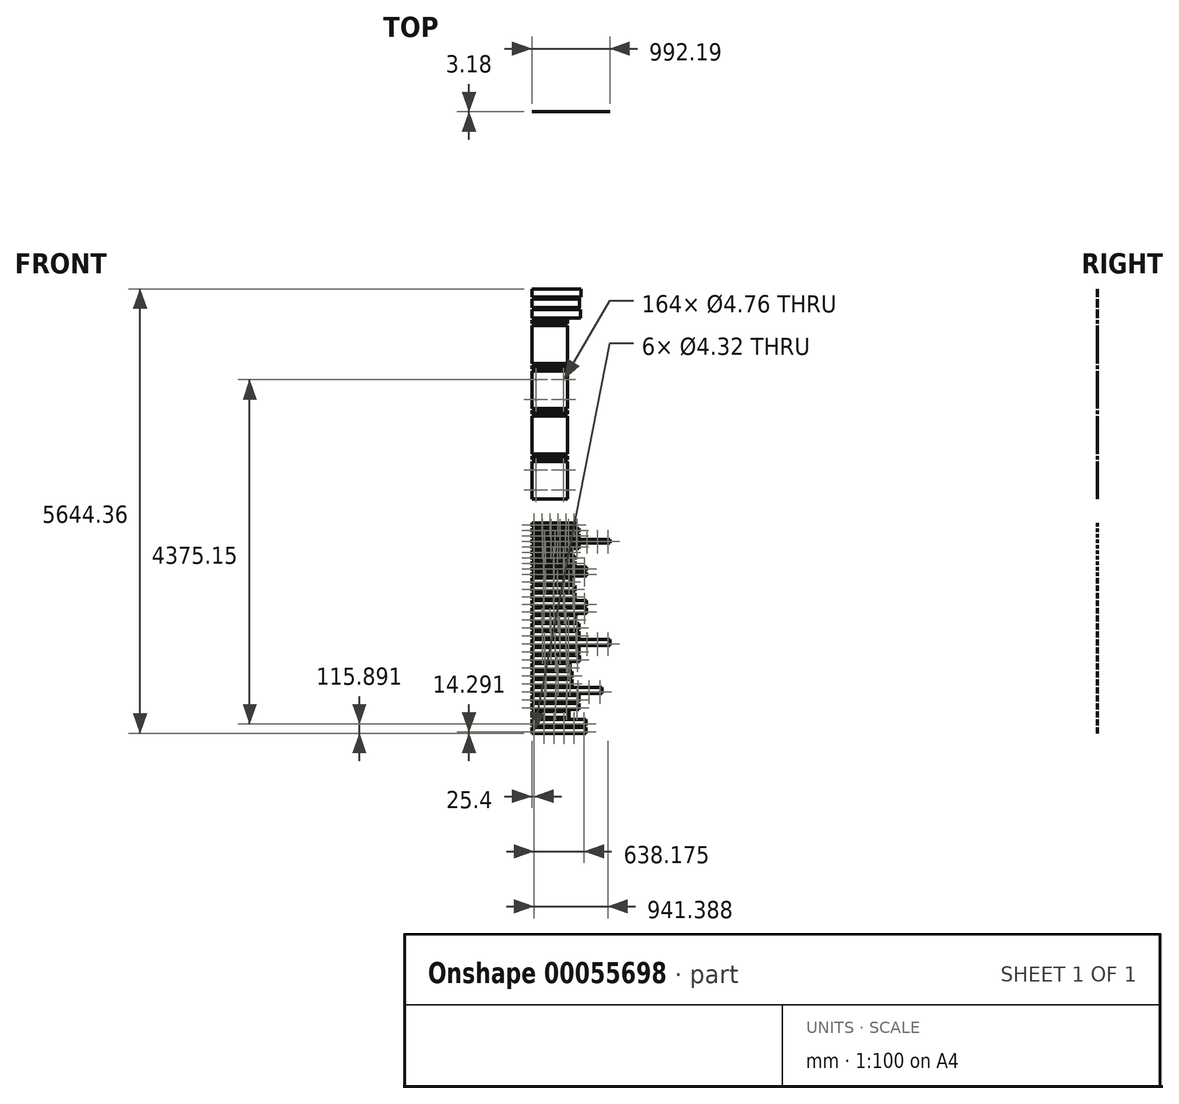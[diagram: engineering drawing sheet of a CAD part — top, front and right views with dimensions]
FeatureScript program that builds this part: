
annotation { "Feature Type Name" : "Feature", "Feature Type Description" : "" }
export const myFeature = defineFeature(function(context is Context, id is Id, definition is map)
    precondition{}
    {
        {
            var Q0;
            Q0=qCreatedBy(makeId("Front.planeOp"),FACE);
            var sketch = newSketch(context, id + "F0", { "sketchPlane" : qUnion([Q0])});
            skLineSegment(sketch, "E0", {"start": v(0, 0) * mm, "end": v(0, -6350) * mm, "construction": true});
            skLineSegment(sketch, "E1.bottom", {"start": v(0, -25.4) * mm, "end": v(621.5, -25.4) * mm});
            skLineSegment(sketch, "E1.top", {"start": v(0, -130.97) * mm, "end": v(621.5, -130.97) * mm});
            skLineSegment(sketch, "E1.left", {"start": v(0, -25.4) * mm, "end": v(0, -130.97) * mm});
            skLineSegment(sketch, "E1.right", {"start": v(621.5, -25.4) * mm, "end": v(621.5, -130.97) * mm});
            skLineSegment(sketch, "E2.bottom", {"start": v(0, -156.37) * mm, "end": v(604.84, -156.37) * mm});
            skLineSegment(sketch, "E2.top", {"start": v(0, -261.94) * mm, "end": v(604.84, -261.94) * mm});
            skLineSegment(sketch, "E2.left", {"start": v(0, -156.37) * mm, "end": v(0, -261.94) * mm});
            skLineSegment(sketch, "E2.right", {"start": v(604.84, -156.37) * mm, "end": v(604.84, -261.94) * mm});
            skLineSegment(sketch, "E3.bottom", {"start": v(0, -287.34) * mm, "end": v(618.33, -287.34) * mm});
            skLineSegment(sketch, "E3.top", {"start": v(0, -392.9) * mm, "end": v(618.33, -392.9) * mm});
            skLineSegment(sketch, "E3.left", {"start": v(0, -287.34) * mm, "end": v(0, -392.9) * mm});
            skLineSegment(sketch, "E3.right", {"start": v(618.33, -287.34) * mm, "end": v(618.33, -392.9) * mm});
            skLineSegment(sketch, "E4.bottom", {"start": v(0, -418.3) * mm, "end": v(454.03, -418.3) * mm});
            skLineSegment(sketch, "E4.top", {"start": v(0, -465.93) * mm, "end": v(454.03, -465.93) * mm});
            skLineSegment(sketch, "E4.left", {"start": v(0, -418.3) * mm, "end": v(0, -465.93) * mm});
            skLineSegment(sketch, "E4.right", {"start": v(454.03, -418.3) * mm, "end": v(454.03, -465.93) * mm});
            skLineSegment(sketch, "E5.bottom", {"start": v(0, -491.33) * mm, "end": v(454.03, -491.33) * mm});
            skLineSegment(sketch, "E5.top", {"start": v(0, -970.76) * mm, "end": v(454.03, -970.76) * mm});
            skLineSegment(sketch, "E5.left", {"start": v(0, -491.33) * mm, "end": v(0, -970.76) * mm});
            skLineSegment(sketch, "E5.right", {"start": v(454.03, -491.33) * mm, "end": v(454.03, -970.76) * mm});
            skLineSegment(sketch, "E6.bottom", {"start": v(0, -996.16) * mm, "end": v(454.03, -996.16) * mm});
            skLineSegment(sketch, "E6.top", {"start": v(0, -1043.78) * mm, "end": v(454.03, -1043.78) * mm});
            skLineSegment(sketch, "E6.left", {"start": v(0, -996.16) * mm, "end": v(0, -1043.78) * mm});
            skLineSegment(sketch, "E6.right", {"start": v(454.03, -996.16) * mm, "end": v(454.03, -1043.78) * mm});
            skLineSegment(sketch, "E7.bottom", {"start": v(0, -1069.18) * mm, "end": v(454.03, -1069.18) * mm});
            skLineSegment(sketch, "E7.top", {"start": v(0, -1542.26) * mm, "end": v(454.03, -1542.26) * mm});
            skLineSegment(sketch, "E7.left", {"start": v(0, -1069.18) * mm, "end": v(0, -1542.26) * mm});
            skLineSegment(sketch, "E7.right", {"start": v(454.03, -1069.18) * mm, "end": v(454.03, -1542.26) * mm});
            skLineSegment(sketch, "E8.bottom", {"start": v(0, -1567.66) * mm, "end": v(454.03, -1567.66) * mm});
            skLineSegment(sketch, "E8.top", {"start": v(0, -1615.28) * mm, "end": v(454.03, -1615.28) * mm});
            skLineSegment(sketch, "E8.left", {"start": v(0, -1567.66) * mm, "end": v(0, -1615.28) * mm});
            skLineSegment(sketch, "E8.right", {"start": v(454.03, -1567.66) * mm, "end": v(454.03, -1615.28) * mm});
            skLineSegment(sketch, "E9.bottom", {"start": v(0, -1640.68) * mm, "end": v(454.03, -1640.68) * mm});
            skLineSegment(sketch, "E9.top", {"start": v(0, -2120.1) * mm, "end": v(454.03, -2120.1) * mm});
            skLineSegment(sketch, "E9.left", {"start": v(0, -1640.68) * mm, "end": v(0, -2120.1) * mm});
            skLineSegment(sketch, "E9.right", {"start": v(454.03, -1640.68) * mm, "end": v(454.03, -2120.1) * mm});
            skLineSegment(sketch, "E10.bottom", {"start": v(0, -2145.5) * mm, "end": v(454.03, -2145.5) * mm});
            skLineSegment(sketch, "E10.top", {"start": v(0, -2193.13) * mm, "end": v(454.03, -2193.13) * mm});
            skLineSegment(sketch, "E10.left", {"start": v(0, -2145.5) * mm, "end": v(0, -2193.13) * mm});
            skLineSegment(sketch, "E10.right", {"start": v(454.03, -2145.5) * mm, "end": v(454.03, -2193.13) * mm});
            skLineSegment(sketch, "E11.bottom", {"start": v(0, -2218.53) * mm, "end": v(454.03, -2218.53) * mm});
            skLineSegment(sketch, "E11.top", {"start": v(0, -2691.6) * mm, "end": v(454.03, -2691.6) * mm});
            skLineSegment(sketch, "E11.left", {"start": v(0, -2218.53) * mm, "end": v(0, -2691.6) * mm});
            skLineSegment(sketch, "E11.right", {"start": v(454.03, -2218.53) * mm, "end": v(454.03, -2691.6) * mm});
            skLineSegment(sketch, "E12.bottom", {"start": v(403.23, -1178.72) * mm, "end": v(50.8, -1178.72) * mm, "construction": true});
            skLineSegment(sketch, "E12.top", {"start": v(403.23, -1432.72) * mm, "end": v(50.8, -1432.72) * mm, "construction": true});
            skLineSegment(sketch, "E12.left", {"start": v(403.23, -1178.72) * mm, "end": v(403.23, -1432.72) * mm, "construction": true});
            skLineSegment(sketch, "E12.right", {"start": v(50.8, -1178.72) * mm, "end": v(50.8, -1432.72) * mm, "construction": true});
            skLineSegment(sketch, "E13.bottom", {"start": v(403.23, -2328.07) * mm, "end": v(50.8, -2328.07) * mm, "construction": true});
            skLineSegment(sketch, "E13.top", {"start": v(403.23, -2582.07) * mm, "end": v(50.8, -2582.07) * mm, "construction": true});
            skLineSegment(sketch, "E13.left", {"start": v(403.22, -2328.07) * mm, "end": v(403.22, -2582.07) * mm, "construction": true});
            skLineSegment(sketch, "E13.right", {"start": v(50.8, -2328.07) * mm, "end": v(50.8, -2582.07) * mm, "construction": true});
            skLineSegment(sketch, "E14", {"start": v(454.03, -1305.72) * mm, "end": v(0, -1305.72) * mm, "construction": true});
            skPoint(sketch, "E15", {"position": v(403.23, -1305.72) * mm});
            skLineSegment(sketch, "E16", {"start": v(454.03, -2455.07) * mm, "end": v(0, -2455.07) * mm, "construction": true});
            skPoint(sketch, "E17", {"position": v(403.23, -2455.07) * mm});
            skCircle(sketch, "E18", {"center": v(403.23, -1178.72) * mm, "radius": 2.38 * mm});
            skCircle(sketch, "E19", {"center": v(403.23, -1432.72) * mm, "radius": 2.38 * mm});
            skCircle(sketch, "E20", {"center": v(403.23, -2328.07) * mm, "radius": 2.38 * mm});
            skCircle(sketch, "E21", {"center": v(403.23, -2582.07) * mm, "radius": 2.38 * mm});
            skCircle(sketch, "E22", {"center": v(50.8, -1178.72) * mm, "radius": 2.38 * mm});
            skCircle(sketch, "E23", {"center": v(50.8, -1432.72) * mm, "radius": 2.38 * mm});
            skCircle(sketch, "E24", {"center": v(50.8, -2328.07) * mm, "radius": 2.38 * mm});
            skCircle(sketch, "E25", {"center": v(50.8, -2582.07) * mm, "radius": 2.38 * mm});
            skLineSegment(sketch, "E26.bottom", {"start": v(0, -4171.16) * mm, "end": v(561.97, -4171.16) * mm});
            skLineSegment(sketch, "E26.top", {"start": v(0, -4247.36) * mm, "end": v(561.97, -4247.36) * mm});
            skLineSegment(sketch, "E26.left", {"start": v(0, -4171.16) * mm, "end": v(0, -4247.36) * mm});
            skLineSegment(sketch, "E26.right", {"start": v(561.97, -4171.16) * mm, "end": v(561.97, -4247.36) * mm});
            skLineSegment(sketch, "E27", {"start": v(25.4, -4233.07) * mm, "end": v(536.57, -4233.07) * mm, "construction": true});
            skCircle(sketch, "E28", {"center": v(25.4, -4233.07) * mm, "radius": 2.38 * mm});
            skCircle(sketch, "E29", {"center": v(127, -4233.07) * mm, "radius": 2.38 * mm});
            skCircle(sketch, "E30", {"center": v(228.6, -4233.07) * mm, "radius": 2.38 * mm});
            skCircle(sketch, "E31", {"center": v(333.37, -4233.07) * mm, "radius": 2.38 * mm});
            skCircle(sketch, "E32", {"center": v(434.97, -4233.07) * mm, "radius": 2.38 * mm});
            skCircle(sketch, "E33", {"center": v(536.57, -4233.07) * mm, "radius": 2.38 * mm});
            skLineSegment(sketch, "E34.bottom", {"start": v(0, -4272.76) * mm, "end": v(596.9, -4272.76) * mm});
            skLineSegment(sketch, "E34.top", {"start": v(0, -4348.96) * mm, "end": v(596.9, -4348.96) * mm});
            skLineSegment(sketch, "E34.left", {"start": v(0, -4272.76) * mm, "end": v(0, -4348.96) * mm});
            skLineSegment(sketch, "E34.right", {"start": v(596.9, -4272.76) * mm, "end": v(596.9, -4348.96) * mm});
            skLineSegment(sketch, "E35", {"start": v(25.4, -4334.67) * mm, "end": v(571.5, -4334.67) * mm, "construction": true});
            skCircle(sketch, "E36", {"center": v(25.4, -4334.67) * mm, "radius": 2.38 * mm});
            skCircle(sketch, "E37", {"center": v(134.94, -4334.67) * mm, "radius": 2.38 * mm});
            skCircle(sketch, "E38", {"center": v(244.47, -4334.67) * mm, "radius": 2.38 * mm});
            skCircle(sketch, "E39", {"center": v(571.5, -4334.67) * mm, "radius": 2.38 * mm});
            skCircle(sketch, "E40", {"center": v(461.96, -4334.67) * mm, "radius": 2.38 * mm});
            skCircle(sketch, "E41", {"center": v(352.42, -4334.67) * mm, "radius": 2.38 * mm});
            skLineSegment(sketch, "E42.bottom", {"start": v(0, -4374.36) * mm, "end": v(598.49, -4374.36) * mm});
            skLineSegment(sketch, "E42.top", {"start": v(0, -4450.56) * mm, "end": v(598.49, -4450.56) * mm});
            skLineSegment(sketch, "E42.left", {"start": v(0, -4374.36) * mm, "end": v(0, -4450.56) * mm});
            skLineSegment(sketch, "E42.right", {"start": v(598.49, -4374.36) * mm, "end": v(598.49, -4450.56) * mm});
            skLineSegment(sketch, "E43", {"start": v(25.4, -4436.27) * mm, "end": v(573.09, -4436.27) * mm, "construction": true});
            skCircle(sketch, "E44", {"center": v(25.4, -4436.27) * mm, "radius": 2.38 * mm});
            skCircle(sketch, "E45", {"center": v(134.94, -4436.27) * mm, "radius": 2.38 * mm});
            skCircle(sketch, "E46", {"center": v(244.47, -4436.27) * mm, "radius": 2.38 * mm});
            skCircle(sketch, "E47", {"center": v(354.01, -4436.27) * mm, "radius": 2.38 * mm});
            skCircle(sketch, "E48", {"center": v(463.55, -4436.27) * mm, "radius": 2.38 * mm});
            skCircle(sketch, "E49", {"center": v(573.09, -4436.27) * mm, "radius": 2.38 * mm});
            skLineSegment(sketch, "E50.bottom", {"start": v(0, -4475.96) * mm, "end": v(992.19, -4475.96) * mm});
            skLineSegment(sketch, "E50.top", {"start": v(0, -4552.16) * mm, "end": v(992.19, -4552.16) * mm});
            skLineSegment(sketch, "E50.left", {"start": v(0, -4475.96) * mm, "end": v(0, -4552.16) * mm});
            skLineSegment(sketch, "E50.right", {"start": v(992.19, -4475.96) * mm, "end": v(992.19, -4552.16) * mm});
            skLineSegment(sketch, "E51", {"start": v(25.4, -4537.87) * mm, "end": v(966.79, -4537.87) * mm, "construction": true});
            skCircle(sketch, "E52", {"center": v(25.4, -4537.87) * mm, "radius": 2.38 * mm});
            skCircle(sketch, "E53", {"center": v(160.34, -4537.87) * mm, "radius": 2.38 * mm});
            skCircle(sketch, "E54", {"center": v(295.27, -4537.87) * mm, "radius": 2.38 * mm});
            skCircle(sketch, "E55", {"center": v(430.21, -4537.87) * mm, "radius": 2.38 * mm});
            skCircle(sketch, "E56", {"center": v(966.79, -4537.87) * mm, "radius": 2.38 * mm});
            skCircle(sketch, "E57", {"center": v(831.85, -4537.87) * mm, "radius": 2.38 * mm});
            skCircle(sketch, "E58", {"center": v(696.91, -4537.87) * mm, "radius": 2.38 * mm});
            skCircle(sketch, "E59", {"center": v(561.97, -4537.87) * mm, "radius": 2.38 * mm});
            skLineSegment(sketch, "E60.bottom", {"start": v(0, -4577.56) * mm, "end": v(595.31, -4577.56) * mm});
            skLineSegment(sketch, "E60.top", {"start": v(0, -4653.76) * mm, "end": v(595.31, -4653.76) * mm});
            skLineSegment(sketch, "E60.left", {"start": v(0, -4577.56) * mm, "end": v(0, -4653.76) * mm});
            skLineSegment(sketch, "E60.right", {"start": v(595.31, -4577.56) * mm, "end": v(595.31, -4653.76) * mm});
            skLineSegment(sketch, "E61", {"start": v(25.4, -4639.47) * mm, "end": v(569.91, -4639.47) * mm, "construction": true});
            skCircle(sketch, "E62", {"center": v(25.4, -4639.47) * mm, "radius": 2.38 * mm});
            skCircle(sketch, "E63", {"center": v(133.35, -4639.47) * mm, "radius": 2.38 * mm});
            skCircle(sketch, "E64", {"center": v(241.3, -4639.47) * mm, "radius": 2.38 * mm});
            skCircle(sketch, "E65", {"center": v(569.91, -4639.47) * mm, "radius": 2.38 * mm});
            skCircle(sketch, "E66", {"center": v(461.96, -4639.47) * mm, "radius": 2.38 * mm});
            skCircle(sketch, "E67", {"center": v(354.01, -4639.47) * mm, "radius": 2.38 * mm});
            skLineSegment(sketch, "E68.bottom", {"start": v(0, -4679.16) * mm, "end": v(604.84, -4679.16) * mm});
            skLineSegment(sketch, "E68.top", {"start": v(0, -4755.36) * mm, "end": v(604.84, -4755.36) * mm});
            skLineSegment(sketch, "E68.left", {"start": v(0, -4679.16) * mm, "end": v(0, -4755.36) * mm});
            skLineSegment(sketch, "E68.right", {"start": v(604.84, -4679.16) * mm, "end": v(604.84, -4755.36) * mm});
            skLineSegment(sketch, "E69", {"start": v(25.4, -4741.07) * mm, "end": v(579.44, -4741.07) * mm, "construction": true});
            skCircle(sketch, "E70", {"center": v(25.4, -4741.07) * mm, "radius": 2.38 * mm});
            skCircle(sketch, "E71", {"center": v(163.51, -4741.07) * mm, "radius": 2.38 * mm});
            skCircle(sketch, "E72", {"center": v(302.42, -4741.07) * mm, "radius": 2.38 * mm});
            skCircle(sketch, "E73", {"center": v(441.32, -4741.07) * mm, "radius": 2.38 * mm});
            skCircle(sketch, "E74", {"center": v(579.44, -4741.07) * mm, "radius": 2.38 * mm});
            skLineSegment(sketch, "E75", {"start": v(163.51, -4715.67) * mm, "end": v(302.42, -4715.67) * mm, "construction": true});
            skLineSegment(sketch, "E76", {"start": v(302.42, -4715.67) * mm, "end": v(441.32, -4715.67) * mm, "construction": true});
            skLineSegment(sketch, "E77.bottom", {"start": v(0, -4780.76) * mm, "end": v(484.19, -4780.76) * mm});
            skLineSegment(sketch, "E77.top", {"start": v(0, -4856.96) * mm, "end": v(484.19, -4856.96) * mm});
            skLineSegment(sketch, "E77.left", {"start": v(0, -4780.76) * mm, "end": v(0, -4856.96) * mm});
            skLineSegment(sketch, "E77.right", {"start": v(484.19, -4780.76) * mm, "end": v(484.19, -4856.96) * mm});
            skLineSegment(sketch, "E78", {"start": v(25.4, -4842.67) * mm, "end": v(458.79, -4842.67) * mm, "construction": true});
            skCircle(sketch, "E79", {"center": v(25.4, -4842.67) * mm, "radius": 2.38 * mm});
            skCircle(sketch, "E80", {"center": v(168.27, -4842.67) * mm, "radius": 2.38 * mm});
            skCircle(sketch, "E81", {"center": v(315.91, -4842.67) * mm, "radius": 2.38 * mm});
            skCircle(sketch, "E82", {"center": v(458.79, -4842.67) * mm, "radius": 2.38 * mm});
            skLineSegment(sketch, "E83.bottom", {"start": v(0, -4882.36) * mm, "end": v(511.17, -4882.36) * mm});
            skLineSegment(sketch, "E83.top", {"start": v(0, -4958.56) * mm, "end": v(511.17, -4958.56) * mm});
            skLineSegment(sketch, "E83.left", {"start": v(0, -4882.36) * mm, "end": v(0, -4958.56) * mm});
            skLineSegment(sketch, "E83.right", {"start": v(511.17, -4882.36) * mm, "end": v(511.17, -4958.56) * mm});
            skLineSegment(sketch, "E84", {"start": v(25.4, -4944.27) * mm, "end": v(485.77, -4944.27) * mm, "construction": true});
            skCircle(sketch, "E85", {"center": v(25.4, -4944.27) * mm, "radius": 2.38 * mm});
            skCircle(sketch, "E86", {"center": v(177.8, -4944.27) * mm, "radius": 2.38 * mm});
            skCircle(sketch, "E87", {"center": v(333.37, -4944.27) * mm, "radius": 2.38 * mm});
            skCircle(sketch, "E88", {"center": v(485.77, -4944.27) * mm, "radius": 2.38 * mm});
            skLineSegment(sketch, "E89.bottom", {"start": v(0, -4983.96) * mm, "end": v(511.17, -4983.96) * mm});
            skLineSegment(sketch, "E89.top", {"start": v(0, -5060.16) * mm, "end": v(511.17, -5060.16) * mm});
            skLineSegment(sketch, "E89.left", {"start": v(0, -4983.96) * mm, "end": v(0, -5060.16) * mm});
            skLineSegment(sketch, "E89.right", {"start": v(511.17, -4983.96) * mm, "end": v(511.17, -5060.16) * mm});
            skLineSegment(sketch, "E90", {"start": v(25.4, -5045.87) * mm, "end": v(485.77, -5045.87) * mm, "construction": true});
            skCircle(sketch, "E91", {"center": v(25.4, -5045.87) * mm, "radius": 2.38 * mm});
            skCircle(sketch, "E92", {"center": v(485.77, -5045.87) * mm, "radius": 2.38 * mm});
            skCircle(sketch, "E93", {"center": v(333.37, -5045.87) * mm, "radius": 2.38 * mm});
            skCircle(sketch, "E94", {"center": v(177.8, -5045.87) * mm, "radius": 2.38 * mm});
            skLineSegment(sketch, "E95.bottom", {"start": v(0, -5085.56) * mm, "end": v(889, -5085.56) * mm});
            skLineSegment(sketch, "E95.top", {"start": v(0, -5161.76) * mm, "end": v(889, -5161.76) * mm});
            skLineSegment(sketch, "E95.left", {"start": v(0, -5085.56) * mm, "end": v(0, -5161.76) * mm});
            skLineSegment(sketch, "E95.right", {"start": v(889, -5085.56) * mm, "end": v(889, -5161.76) * mm});
            skLineSegment(sketch, "E96", {"start": v(25.4, -5147.47) * mm, "end": v(863.6, -5147.47) * mm, "construction": true});
            skCircle(sketch, "E97", {"center": v(25.4, -5147.47) * mm, "radius": 2.38 * mm});
            skCircle(sketch, "E98", {"center": v(165.1, -5147.47) * mm, "radius": 2.38 * mm});
            skCircle(sketch, "E99", {"center": v(304.8, -5147.47) * mm, "radius": 2.38 * mm});
            skCircle(sketch, "E100", {"center": v(444.5, -5147.47) * mm, "radius": 2.38 * mm});
            skCircle(sketch, "E101", {"center": v(584.2, -5147.47) * mm, "radius": 2.38 * mm});
            skCircle(sketch, "E102", {"center": v(723.9, -5147.47) * mm, "radius": 2.38 * mm});
            skCircle(sketch, "E103", {"center": v(863.6, -5147.47) * mm, "radius": 2.38 * mm});
            skLineSegment(sketch, "E104", {"start": v(304.8, -5122.07) * mm, "end": v(444.5, -5122.07) * mm, "construction": true});
            skLineSegment(sketch, "E105", {"start": v(444.5, -5122.07) * mm, "end": v(584.2, -5122.07) * mm, "construction": true});
            skLineSegment(sketch, "E106.bottom", {"start": v(0, -5187.16) * mm, "end": v(600.07, -5187.16) * mm});
            skLineSegment(sketch, "E106.top", {"start": v(0, -5263.36) * mm, "end": v(600.07, -5263.36) * mm});
            skLineSegment(sketch, "E106.left", {"start": v(0, -5187.16) * mm, "end": v(0, -5263.36) * mm});
            skLineSegment(sketch, "E106.right", {"start": v(600.07, -5187.16) * mm, "end": v(600.07, -5263.36) * mm});
            skLineSegment(sketch, "E107", {"start": v(25.4, -5249.07) * mm, "end": v(574.67, -5249.07) * mm, "construction": true});
            skCircle(sketch, "E108", {"center": v(25.4, -5249.07) * mm, "radius": 2.38 * mm});
            skCircle(sketch, "E109", {"center": v(161.92, -5249.07) * mm, "radius": 2.38 * mm});
            skCircle(sketch, "E110", {"center": v(300.04, -5249.07) * mm, "radius": 2.38 * mm});
            skCircle(sketch, "E111", {"center": v(438.15, -5249.07) * mm, "radius": 2.38 * mm});
            skCircle(sketch, "E112", {"center": v(574.67, -5249.07) * mm, "radius": 2.38 * mm});
            skLineSegment(sketch, "E113", {"start": v(161.92, -5223.67) * mm, "end": v(300.04, -5223.67) * mm, "construction": true});
            skLineSegment(sketch, "E114", {"start": v(300.04, -5223.67) * mm, "end": v(438.15, -5223.67) * mm, "construction": true});
            skLineSegment(sketch, "E115.bottom", {"start": v(0, -5288.76) * mm, "end": v(600.07, -5288.76) * mm});
            skLineSegment(sketch, "E115.top", {"start": v(0, -5364.96) * mm, "end": v(600.07, -5364.96) * mm});
            skLineSegment(sketch, "E115.left", {"start": v(0, -5288.76) * mm, "end": v(0, -5364.96) * mm});
            skLineSegment(sketch, "E115.right", {"start": v(600.07, -5288.76) * mm, "end": v(600.07, -5364.96) * mm});
            skLineSegment(sketch, "E116", {"start": v(25.4, -5350.67) * mm, "end": v(574.67, -5350.67) * mm, "construction": true});
            skCircle(sketch, "E117", {"center": v(25.4, -5350.67) * mm, "radius": 2.38 * mm});
            skCircle(sketch, "E118", {"center": v(161.92, -5350.67) * mm, "radius": 2.38 * mm});
            skCircle(sketch, "E119", {"center": v(300.04, -5350.67) * mm, "radius": 2.38 * mm});
            skCircle(sketch, "E120", {"center": v(438.15, -5350.67) * mm, "radius": 2.38 * mm});
            skCircle(sketch, "E121", {"center": v(574.67, -5350.67) * mm, "radius": 2.38 * mm});
            skLineSegment(sketch, "E122", {"start": v(161.92, -5325.27) * mm, "end": v(300.04, -5325.27) * mm, "construction": true});
            skLineSegment(sketch, "E123", {"start": v(300.04, -5325.27) * mm, "end": v(438.15, -5325.27) * mm, "construction": true});
            skLineSegment(sketch, "E124.bottom", {"start": v(0, -5390.36) * mm, "end": v(473.07, -5390.36) * mm});
            skLineSegment(sketch, "E124.top", {"start": v(0, -5466.56) * mm, "end": v(473.07, -5466.56) * mm});
            skLineSegment(sketch, "E124.left", {"start": v(0, -5390.36) * mm, "end": v(0, -5466.56) * mm});
            skLineSegment(sketch, "E124.right", {"start": v(473.07, -5390.36) * mm, "end": v(473.07, -5466.56) * mm});
            skLineSegment(sketch, "E125.bottom", {"start": v(0, -5491.96) * mm, "end": v(688.97, -5491.96) * mm});
            skLineSegment(sketch, "E125.top", {"start": v(0, -5568.16) * mm, "end": v(688.97, -5568.16) * mm});
            skLineSegment(sketch, "E125.left", {"start": v(0, -5491.96) * mm, "end": v(0, -5568.16) * mm});
            skLineSegment(sketch, "E125.right", {"start": v(688.97, -5491.96) * mm, "end": v(688.97, -5568.16) * mm});
            skLineSegment(sketch, "E126", {"start": v(25.4, -5553.87) * mm, "end": v(663.57, -5553.87) * mm, "construction": true});
            skCircle(sketch, "E127", {"center": v(25.4, -5553.87) * mm, "radius": 2.38 * mm});
            skCircle(sketch, "E128", {"center": v(663.57, -5553.87) * mm, "radius": 2.38 * mm});
            skCircle(sketch, "E129", {"center": v(152.4, -5553.87) * mm, "radius": 2.38 * mm});
            skCircle(sketch, "E130", {"center": v(279.4, -5553.87) * mm, "radius": 2.38 * mm});
            skCircle(sketch, "E131", {"center": v(409.57, -5553.87) * mm, "radius": 2.38 * mm});
            skCircle(sketch, "E132", {"center": v(536.57, -5553.87) * mm, "radius": 2.38 * mm});
            skLineSegment(sketch, "E133.bottom", {"start": v(0, -5593.56) * mm, "end": v(688.97, -5593.56) * mm});
            skLineSegment(sketch, "E133.top", {"start": v(0, -5669.76) * mm, "end": v(688.97, -5669.76) * mm});
            skLineSegment(sketch, "E133.left", {"start": v(0, -5593.56) * mm, "end": v(0, -5669.76) * mm});
            skLineSegment(sketch, "E133.right", {"start": v(688.98, -5593.56) * mm, "end": v(688.98, -5669.76) * mm});
            skLineSegment(sketch, "E134", {"start": v(25.4, -5655.47) * mm, "end": v(663.57, -5655.47) * mm, "construction": true});
            skCircle(sketch, "E135", {"center": v(25.4, -5655.47) * mm, "radius": 2.16 * mm});
            skCircle(sketch, "E136", {"center": v(663.57, -5655.47) * mm, "radius": 2.16 * mm});
            skCircle(sketch, "E137", {"center": v(152.4, -5655.47) * mm, "radius": 2.16 * mm});
            skCircle(sketch, "E138", {"center": v(279.4, -5655.47) * mm, "radius": 2.16 * mm});
            skCircle(sketch, "E139", {"center": v(409.57, -5655.47) * mm, "radius": 2.16 * mm});
            skCircle(sketch, "E140", {"center": v(536.57, -5655.47) * mm, "radius": 2.16 * mm});
            skLineSegment(sketch, "E141.bottom", {"start": v(0, -2996.4) * mm, "end": v(561.97, -2996.4) * mm});
            skLineSegment(sketch, "E141.top", {"start": v(0, -3040.86) * mm, "end": v(561.97, -3040.86) * mm});
            skLineSegment(sketch, "E141.left", {"start": v(0, -2996.4) * mm, "end": v(0, -3040.86) * mm});
            skLineSegment(sketch, "E141.right", {"start": v(561.97, -2996.4) * mm, "end": v(561.97, -3040.86) * mm});
            skLineSegment(sketch, "E142", {"start": v(25.4, -3026.57) * mm, "end": v(536.57, -3026.57) * mm, "construction": true});
            skCircle(sketch, "E143", {"center": v(25.4, -3026.57) * mm, "radius": 2.38 * mm});
            skCircle(sketch, "E144", {"center": v(127, -3026.57) * mm, "radius": 2.38 * mm});
            skCircle(sketch, "E145", {"center": v(228.6, -3026.57) * mm, "radius": 2.38 * mm});
            skCircle(sketch, "E146", {"center": v(536.57, -3026.57) * mm, "radius": 2.38 * mm});
            skCircle(sketch, "E147", {"center": v(434.97, -3026.57) * mm, "radius": 2.38 * mm});
            skCircle(sketch, "E148", {"center": v(333.37, -3026.57) * mm, "radius": 2.38 * mm});
            skLineSegment(sketch, "E149.bottom", {"start": v(0, -3066.26) * mm, "end": v(596.9, -3066.26) * mm});
            skLineSegment(sketch, "E149.top", {"start": v(0, -3110.7) * mm, "end": v(596.9, -3110.7) * mm});
            skLineSegment(sketch, "E149.left", {"start": v(0, -3066.26) * mm, "end": v(0, -3110.7) * mm});
            skLineSegment(sketch, "E149.right", {"start": v(596.9, -3066.26) * mm, "end": v(596.9, -3110.7) * mm});
            skLineSegment(sketch, "E150", {"start": v(25.4, -3096.42) * mm, "end": v(571.5, -3096.42) * mm, "construction": true});
            skCircle(sketch, "E151", {"center": v(25.4, -3096.42) * mm, "radius": 2.38 * mm});
            skCircle(sketch, "E152", {"center": v(133.35, -3096.42) * mm, "radius": 2.38 * mm});
            skCircle(sketch, "E153", {"center": v(241.3, -3096.42) * mm, "radius": 2.38 * mm});
            skCircle(sketch, "E154", {"center": v(571.5, -3096.42) * mm, "radius": 2.38 * mm});
            skCircle(sketch, "E155", {"center": v(463.55, -3096.42) * mm, "radius": 2.38 * mm});
            skCircle(sketch, "E156", {"center": v(355.6, -3096.42) * mm, "radius": 2.38 * mm});
            skLineSegment(sketch, "E157.bottom", {"start": v(0, -3136.1) * mm, "end": v(598.49, -3136.1) * mm});
            skLineSegment(sketch, "E157.top", {"start": v(0, -3180.56) * mm, "end": v(598.49, -3180.56) * mm});
            skLineSegment(sketch, "E157.left", {"start": v(0, -3136.1) * mm, "end": v(0, -3180.56) * mm});
            skLineSegment(sketch, "E157.right", {"start": v(598.49, -3136.1) * mm, "end": v(598.49, -3180.56) * mm});
            skLineSegment(sketch, "E158", {"start": v(25.4, -3166.27) * mm, "end": v(573.09, -3166.27) * mm, "construction": true});
            skCircle(sketch, "E159", {"center": v(25.4, -3166.27) * mm, "radius": 2.38 * mm});
            skCircle(sketch, "E160", {"center": v(134.94, -3166.27) * mm, "radius": 2.38 * mm});
            skCircle(sketch, "E161", {"center": v(244.47, -3166.27) * mm, "radius": 2.38 * mm});
            skCircle(sketch, "E162", {"center": v(573.09, -3166.27) * mm, "radius": 2.38 * mm});
            skCircle(sketch, "E163", {"center": v(463.55, -3166.27) * mm, "radius": 2.38 * mm});
            skCircle(sketch, "E164", {"center": v(354.01, -3166.27) * mm, "radius": 2.38 * mm});
            skLineSegment(sketch, "E165.bottom", {"start": v(0, -3205.96) * mm, "end": v(992.19, -3205.96) * mm});
            skLineSegment(sketch, "E165.top", {"start": v(0, -3250.4) * mm, "end": v(992.19, -3250.4) * mm});
            skLineSegment(sketch, "E165.left", {"start": v(0, -3205.96) * mm, "end": v(0, -3250.4) * mm});
            skLineSegment(sketch, "E165.right", {"start": v(992.19, -3205.96) * mm, "end": v(992.19, -3250.4) * mm});
            skLineSegment(sketch, "E166.bottom", {"start": v(0, -3275.8) * mm, "end": v(595.31, -3275.8) * mm});
            skLineSegment(sketch, "E166.top", {"start": v(0, -3320.26) * mm, "end": v(595.31, -3320.26) * mm});
            skLineSegment(sketch, "E166.left", {"start": v(0, -3275.8) * mm, "end": v(0, -3320.26) * mm});
            skLineSegment(sketch, "E166.right", {"start": v(595.31, -3275.8) * mm, "end": v(595.31, -3320.26) * mm});
            skLineSegment(sketch, "E167.bottom", {"start": v(0, -3345.66) * mm, "end": v(495.3, -3345.66) * mm});
            skLineSegment(sketch, "E167.top", {"start": v(0, -3390.1) * mm, "end": v(495.3, -3390.1) * mm});
            skLineSegment(sketch, "E167.left", {"start": v(0, -3345.66) * mm, "end": v(0, -3390.1) * mm});
            skLineSegment(sketch, "E167.right", {"start": v(495.3, -3345.66) * mm, "end": v(495.3, -3390.1) * mm});
            skLineSegment(sketch, "E168.bottom", {"start": v(0, -3415.5) * mm, "end": v(547.69, -3415.5) * mm});
            skLineSegment(sketch, "E168.top", {"start": v(0, -3459.96) * mm, "end": v(547.69, -3459.96) * mm});
            skLineSegment(sketch, "E168.left", {"start": v(0, -3415.5) * mm, "end": v(0, -3459.96) * mm});
            skLineSegment(sketch, "E168.right", {"start": v(547.69, -3415.5) * mm, "end": v(547.69, -3459.96) * mm});
            skLineSegment(sketch, "E169.bottom", {"start": v(0, -3485.36) * mm, "end": v(547.69, -3485.36) * mm});
            skLineSegment(sketch, "E169.top", {"start": v(0, -3529.8) * mm, "end": v(547.69, -3529.8) * mm});
            skLineSegment(sketch, "E169.left", {"start": v(0, -3485.36) * mm, "end": v(0, -3529.8) * mm});
            skLineSegment(sketch, "E169.right", {"start": v(547.69, -3485.36) * mm, "end": v(547.69, -3529.8) * mm});
            skLineSegment(sketch, "E170.bottom", {"start": v(0, -3555.2) * mm, "end": v(695.32, -3555.2) * mm});
            skLineSegment(sketch, "E170.top", {"start": v(0, -3599.66) * mm, "end": v(695.32, -3599.66) * mm});
            skLineSegment(sketch, "E170.left", {"start": v(0, -3555.2) * mm, "end": v(0, -3599.66) * mm});
            skLineSegment(sketch, "E170.right", {"start": v(695.32, -3555.2) * mm, "end": v(695.32, -3599.66) * mm});
            skLineSegment(sketch, "E171.bottom", {"start": v(0, -3625.06) * mm, "end": v(695.32, -3625.06) * mm});
            skLineSegment(sketch, "E171.top", {"start": v(0, -3669.5) * mm, "end": v(695.32, -3669.5) * mm});
            skLineSegment(sketch, "E171.left", {"start": v(0, -3625.06) * mm, "end": v(0, -3669.5) * mm});
            skLineSegment(sketch, "E171.right", {"start": v(695.32, -3625.06) * mm, "end": v(695.32, -3669.5) * mm});
            skLineSegment(sketch, "E172.bottom", {"start": v(0, -3694.9) * mm, "end": v(495.3, -3694.9) * mm});
            skLineSegment(sketch, "E172.top", {"start": v(0, -3764.76) * mm, "end": v(495.3, -3764.76) * mm});
            skLineSegment(sketch, "E172.left", {"start": v(0, -3694.9) * mm, "end": v(0, -3764.76) * mm});
            skLineSegment(sketch, "E172.right", {"start": v(495.3, -3694.9) * mm, "end": v(495.3, -3764.76) * mm});
            skLineSegment(sketch, "E173.bottom", {"start": v(0, -3790.16) * mm, "end": v(547.69, -3790.16) * mm});
            skLineSegment(sketch, "E173.top", {"start": v(0, -3860) * mm, "end": v(547.69, -3860) * mm});
            skLineSegment(sketch, "E173.left", {"start": v(0, -3790.16) * mm, "end": v(0, -3860) * mm});
            skLineSegment(sketch, "E173.right", {"start": v(547.69, -3790.16) * mm, "end": v(547.69, -3860) * mm});
            skLineSegment(sketch, "E174.bottom", {"start": v(0, -3885.4) * mm, "end": v(547.69, -3885.4) * mm});
            skLineSegment(sketch, "E174.top", {"start": v(0, -3955.26) * mm, "end": v(547.69, -3955.26) * mm});
            skLineSegment(sketch, "E174.left", {"start": v(0, -3885.4) * mm, "end": v(0, -3955.26) * mm});
            skLineSegment(sketch, "E174.right", {"start": v(547.69, -3885.4) * mm, "end": v(547.69, -3955.26) * mm});
            skLineSegment(sketch, "E175.bottom", {"start": v(0, -3980.66) * mm, "end": v(695.32, -3980.66) * mm});
            skLineSegment(sketch, "E175.top", {"start": v(0, -4050.5) * mm, "end": v(695.32, -4050.5) * mm});
            skLineSegment(sketch, "E175.left", {"start": v(0, -3980.66) * mm, "end": v(0, -4050.5) * mm});
            skLineSegment(sketch, "E175.right", {"start": v(695.32, -3980.66) * mm, "end": v(695.32, -4050.5) * mm});
            skLineSegment(sketch, "E176.bottom", {"start": v(0, -4075.9) * mm, "end": v(695.32, -4075.9) * mm});
            skLineSegment(sketch, "E176.top", {"start": v(0, -4145.76) * mm, "end": v(695.32, -4145.76) * mm});
            skLineSegment(sketch, "E176.left", {"start": v(0, -4075.9) * mm, "end": v(0, -4145.76) * mm});
            skLineSegment(sketch, "E176.right", {"start": v(695.32, -4075.9) * mm, "end": v(695.32, -4145.76) * mm});
            skLineSegment(sketch, "E177", {"start": v(25.4, -3236.12) * mm, "end": v(966.79, -3236.12) * mm, "construction": true});
            skCircle(sketch, "E178", {"center": v(25.4, -3236.12) * mm, "radius": 2.38 * mm});
            skCircle(sketch, "E179", {"center": v(158.75, -3236.12) * mm, "radius": 2.38 * mm});
            skCircle(sketch, "E180", {"center": v(292.1, -3236.12) * mm, "radius": 2.38 * mm});
            skCircle(sketch, "E181", {"center": v(425.45, -3236.12) * mm, "radius": 2.38 * mm});
            skCircle(sketch, "E182", {"center": v(966.79, -3236.12) * mm, "radius": 2.38 * mm});
            skCircle(sketch, "E183", {"center": v(833.44, -3236.12) * mm, "radius": 2.38 * mm});
            skCircle(sketch, "E184", {"center": v(566.74, -3236.12) * mm, "radius": 2.38 * mm});
            skCircle(sketch, "E185", {"center": v(700.09, -3236.12) * mm, "radius": 2.38 * mm});
            skLineSegment(sketch, "E186", {"start": v(25.4, -3305.97) * mm, "end": v(569.91, -3305.97) * mm, "construction": true});
            skCircle(sketch, "E187", {"center": v(25.4, -3305.97) * mm, "radius": 2.38 * mm});
            skCircle(sketch, "E188", {"center": v(133.35, -3305.97) * mm, "radius": 2.38 * mm});
            skCircle(sketch, "E189", {"center": v(241.3, -3305.97) * mm, "radius": 2.38 * mm});
            skCircle(sketch, "E190", {"center": v(569.91, -3305.97) * mm, "radius": 2.38 * mm});
            skCircle(sketch, "E191", {"center": v(461.96, -3305.97) * mm, "radius": 2.38 * mm});
            skCircle(sketch, "E192", {"center": v(354.01, -3305.97) * mm, "radius": 2.38 * mm});
            skLineSegment(sketch, "E193", {"start": v(25.4, -3375.82) * mm, "end": v(469.9, -3375.82) * mm, "construction": true});
            skCircle(sketch, "E194", {"center": v(25.4, -3375.82) * mm, "radius": 2.38 * mm});
            skCircle(sketch, "E195", {"center": v(173.04, -3375.82) * mm, "radius": 2.38 * mm});
            skCircle(sketch, "E196", {"center": v(469.9, -3375.82) * mm, "radius": 2.38 * mm});
            skCircle(sketch, "E197", {"center": v(322.26, -3375.82) * mm, "radius": 2.38 * mm});
            skLineSegment(sketch, "E198", {"start": v(25.4, -3445.67) * mm, "end": v(522.29, -3445.67) * mm, "construction": true});
            skCircle(sketch, "E199", {"center": v(25.4, -3445.67) * mm, "radius": 2.38 * mm});
            skCircle(sketch, "E200", {"center": v(149.22, -3445.67) * mm, "radius": 2.38 * mm});
            skCircle(sketch, "E201", {"center": v(273.84, -3445.67) * mm, "radius": 2.38 * mm});
            skCircle(sketch, "E202", {"center": v(398.46, -3445.67) * mm, "radius": 2.38 * mm});
            skCircle(sketch, "E203", {"center": v(522.29, -3445.67) * mm, "radius": 2.38 * mm});
            skLineSegment(sketch, "E204", {"start": v(25.4, -3515.52) * mm, "end": v(522.29, -3515.52) * mm, "construction": true});
            skCircle(sketch, "E205", {"center": v(25.4, -3515.52) * mm, "radius": 2.38 * mm});
            skCircle(sketch, "E206", {"center": v(149.22, -3515.52) * mm, "radius": 2.38 * mm});
            skCircle(sketch, "E207", {"center": v(273.84, -3515.52) * mm, "radius": 2.38 * mm});
            skCircle(sketch, "E208", {"center": v(398.46, -3515.52) * mm, "radius": 2.38 * mm});
            skCircle(sketch, "E209", {"center": v(522.29, -3515.52) * mm, "radius": 2.38 * mm});
            skLineSegment(sketch, "E210", {"start": v(25.4, -3585.37) * mm, "end": v(669.92, -3585.37) * mm, "construction": true});
            skCircle(sketch, "E211", {"center": v(25.4, -3585.37) * mm, "radius": 2.38 * mm});
            skCircle(sketch, "E212", {"center": v(153.99, -3585.37) * mm, "radius": 2.38 * mm});
            skCircle(sketch, "E213", {"center": v(282.57, -3585.37) * mm, "radius": 2.38 * mm});
            skCircle(sketch, "E214", {"center": v(669.92, -3585.37) * mm, "radius": 2.38 * mm});
            skCircle(sketch, "E215", {"center": v(541.34, -3585.37) * mm, "radius": 2.38 * mm});
            skCircle(sketch, "E216", {"center": v(412.75, -3585.37) * mm, "radius": 2.38 * mm});
            skLineSegment(sketch, "E217", {"start": v(25.4, -3655.22) * mm, "end": v(669.92, -3655.22) * mm, "construction": true});
            skCircle(sketch, "E218", {"center": v(25.4, -3655.22) * mm, "radius": 2.38 * mm});
            skCircle(sketch, "E219", {"center": v(669.92, -3655.22) * mm, "radius": 2.38 * mm});
            skCircle(sketch, "E220", {"center": v(152.4, -3655.22) * mm, "radius": 2.38 * mm});
            skCircle(sketch, "E221", {"center": v(279.4, -3655.22) * mm, "radius": 2.38 * mm});
            skCircle(sketch, "E222", {"center": v(415.92, -3655.22) * mm, "radius": 2.38 * mm});
            skCircle(sketch, "E223", {"center": v(542.92, -3655.22) * mm, "radius": 2.38 * mm});
            skLineSegment(sketch, "E224", {"start": v(25.4, -3750.47) * mm, "end": v(469.9, -3750.47) * mm, "construction": true});
            skCircle(sketch, "E225", {"center": v(25.4, -3750.47) * mm, "radius": 2.38 * mm});
            skCircle(sketch, "E226", {"center": v(173.04, -3750.47) * mm, "radius": 2.38 * mm});
            skCircle(sketch, "E227", {"center": v(322.26, -3750.47) * mm, "radius": 2.38 * mm});
            skCircle(sketch, "E228", {"center": v(469.9, -3750.47) * mm, "radius": 2.38 * mm});
            skLineSegment(sketch, "E229", {"start": v(25.4, -3845.72) * mm, "end": v(522.29, -3845.72) * mm, "construction": true});
            skCircle(sketch, "E230", {"center": v(25.4, -3845.72) * mm, "radius": 2.38 * mm});
            skCircle(sketch, "E231", {"center": v(149.22, -3845.72) * mm, "radius": 2.38 * mm});
            skCircle(sketch, "E232", {"center": v(273.84, -3845.72) * mm, "radius": 2.38 * mm});
            skCircle(sketch, "E233", {"center": v(398.46, -3845.72) * mm, "radius": 2.38 * mm});
            skCircle(sketch, "E234", {"center": v(522.29, -3845.72) * mm, "radius": 2.38 * mm});
            skLineSegment(sketch, "E235", {"start": v(25.4, -3940.97) * mm, "end": v(522.29, -3940.97) * mm, "construction": true});
            skCircle(sketch, "E236", {"center": v(25.4, -3940.97) * mm, "radius": 2.38 * mm});
            skCircle(sketch, "E237", {"center": v(149.22, -3940.97) * mm, "radius": 2.38 * mm});
            skCircle(sketch, "E238", {"center": v(273.84, -3940.97) * mm, "radius": 2.38 * mm});
            skCircle(sketch, "E239", {"center": v(398.46, -3940.97) * mm, "radius": 2.38 * mm});
            skCircle(sketch, "E240", {"center": v(522.29, -3940.97) * mm, "radius": 2.38 * mm});
            skLineSegment(sketch, "E241", {"start": v(25.4, -4036.22) * mm, "end": v(669.92, -4036.22) * mm, "construction": true});
            skLineSegment(sketch, "E242", {"start": v(25.4, -4131.47) * mm, "end": v(669.92, -4131.47) * mm, "construction": true});
            skCircle(sketch, "E243", {"center": v(25.4, -4036.22) * mm, "radius": 2.38 * mm});
            skCircle(sketch, "E244", {"center": v(153.99, -4036.22) * mm, "radius": 2.38 * mm});
            skCircle(sketch, "E245", {"center": v(282.57, -4036.22) * mm, "radius": 2.38 * mm});
            skCircle(sketch, "E246", {"center": v(412.75, -4036.22) * mm, "radius": 2.38 * mm});
            skCircle(sketch, "E247", {"center": v(541.34, -4036.22) * mm, "radius": 2.38 * mm});
            skCircle(sketch, "E248", {"center": v(669.92, -4036.22) * mm, "radius": 2.38 * mm});
            skCircle(sketch, "E249", {"center": v(25.4, -4131.47) * mm, "radius": 2.38 * mm});
            skCircle(sketch, "E250", {"center": v(153.99, -4131.47) * mm, "radius": 2.38 * mm});
            skCircle(sketch, "E251", {"center": v(282.57, -4131.47) * mm, "radius": 2.38 * mm});
            skCircle(sketch, "E252", {"center": v(412.75, -4131.47) * mm, "radius": 2.38 * mm});
            skCircle(sketch, "E253", {"center": v(541.34, -4131.47) * mm, "radius": 2.38 * mm});
            skCircle(sketch, "E254", {"center": v(669.92, -4131.47) * mm, "radius": 2.38 * mm});
            skSolve(sketch);
        }
        {
            var Q0;
            Q0=makeQuery(id+"F0.imprint","IMPRINT",FACE,{"disambiguationData":[TD([[makeQuery(id+"F0.imprint","IMPRINT",EDGE,{"derivedFrom":sQuery(id+"F0.wireOp",EDGE,"E1.bottom")}),-1.0]])]});
            var Q1;
            Q1=makeQuery(id+"F0.imprint","IMPRINT",FACE,{"disambiguationData":[TD([[makeQuery(id+"F0.imprint","IMPRINT",EDGE,{"derivedFrom":sQuery(id+"F0.wireOp",EDGE,"E2.bottom")}),-1.0]])]});
            var Q2;
            Q2=makeQuery(id+"F0.imprint","IMPRINT",FACE,{"disambiguationData":[TD([[makeQuery(id+"F0.imprint","IMPRINT",EDGE,{"derivedFrom":sQuery(id+"F0.wireOp",EDGE,"E3.bottom")}),-1.0]])]});
            var Q3;
            Q3=makeQuery(id+"F0.imprint","IMPRINT",FACE,{"disambiguationData":[TD([[makeQuery(id+"F0.imprint","IMPRINT",EDGE,{"derivedFrom":sQuery(id+"F0.wireOp",EDGE,"22f3f217-47f0-4172-9fc4-0574ea6635b7.bottom")}),-1.0]])]});
            var Q4;
            Q4=makeQuery(id+"F0.imprint","IMPRINT",FACE,{"disambiguationData":[TD([[makeQuery(id+"F0.imprint","IMPRINT",EDGE,{"derivedFrom":sQuery(id+"F0.wireOp",EDGE,"72fb418b-1402-4fbf-a07a-5a8621be927d.bottom")}),-1.0]])]});
            var Q5;
            Q5=makeQuery(id+"F0.imprint","IMPRINT",FACE,{"disambiguationData":[TD([[makeQuery(id+"F0.imprint","IMPRINT",EDGE,{"derivedFrom":sQuery(id+"F0.wireOp",EDGE,"a4b96818-7de0-487c-b4de-a9d5d789bc6b.bottom")}),-1.0]])]});
            var Q6;
            Q6=makeQuery(id+"F0.imprint","IMPRINT",FACE,{"disambiguationData":[TD([[makeQuery(id+"F0.imprint","IMPRINT",EDGE,{"derivedFrom":sQuery(id+"F0.wireOp",EDGE,"acbed7c6-ec86-4632-a830-18483c4dc695.bottom")}),-1.0]])]});
            var Q7;
            Q7=makeQuery(id+"F0.imprint","IMPRINT",FACE,{"disambiguationData":[TD([[makeQuery(id+"F0.imprint","IMPRINT",EDGE,{"derivedFrom":sQuery(id+"F0.wireOp",EDGE,"f84e1fee-73da-47fd-8cfa-b99ec92ecab5.bottom")}),-1.0]])]});
            var Q8;
            Q8=makeQuery(id+"F0.imprint","IMPRINT",FACE,{"disambiguationData":[TD([[makeQuery(id+"F0.imprint","IMPRINT",EDGE,{"derivedFrom":sQuery(id+"F0.wireOp",EDGE,"E4.bottom")}),-1.0]])]});
            var Q9;
            Q9=makeQuery(id+"F0.imprint","IMPRINT",FACE,{"disambiguationData":[TD([[makeQuery(id+"F0.imprint","IMPRINT",EDGE,{"derivedFrom":sQuery(id+"F0.wireOp",EDGE,"E5.bottom")}),-1.0]])]});
            var Q10;
            Q10=makeQuery(id+"F0.imprint","IMPRINT",FACE,{"disambiguationData":[TD([[makeQuery(id+"F0.imprint","IMPRINT",EDGE,{"derivedFrom":sQuery(id+"F0.wireOp",EDGE,"E6.bottom")}),-1.0]])]});
            var Q11;
            Q11=makeQuery(id+"F0.imprint","IMPRINT",FACE,{"disambiguationData":[TD([[makeQuery(id+"F0.imprint","IMPRINT",EDGE,{"derivedFrom":sQuery(id+"F0.wireOp",EDGE,"E7.bottom")}),-1.0]])]});
            var Q12;
            Q12=makeQuery(id+"F0.imprint","IMPRINT",FACE,{"disambiguationData":[TD([[makeQuery(id+"F0.imprint","IMPRINT",EDGE,{"derivedFrom":sQuery(id+"F0.wireOp",EDGE,"E8.bottom")}),-1.0]])]});
            var Q13;
            Q13=makeQuery(id+"F0.imprint","IMPRINT",FACE,{"disambiguationData":[TD([[makeQuery(id+"F0.imprint","IMPRINT",EDGE,{"derivedFrom":sQuery(id+"F0.wireOp",EDGE,"E9.bottom")}),-1.0]])]});
            var Q14;
            Q14=makeQuery(id+"F0.imprint","IMPRINT",FACE,{"disambiguationData":[TD([[makeQuery(id+"F0.imprint","IMPRINT",EDGE,{"derivedFrom":sQuery(id+"F0.wireOp",EDGE,"E10.bottom")}),-1.0]])]});
            var Q15;
            Q15=makeQuery(id+"F0.imprint","IMPRINT",FACE,{"disambiguationData":[TD([[makeQuery(id+"F0.imprint","IMPRINT",EDGE,{"derivedFrom":sQuery(id+"F0.wireOp",EDGE,"E11.bottom")}),-1.0]])]});
            var Q16;
            Q16=makeQuery(id+"F0.imprint","IMPRINT",FACE,{"disambiguationData":[TD([[makeQuery(id+"F0.imprint","IMPRINT",EDGE,{"derivedFrom":sQuery(id+"F0.wireOp",EDGE,"E26.bottom")}),-1.0]])]});
            var Q17;
            Q17=makeQuery(id+"F0.imprint","IMPRINT",FACE,{"disambiguationData":[TD([[makeQuery(id+"F0.imprint","IMPRINT",EDGE,{"derivedFrom":sQuery(id+"F0.wireOp",EDGE,"E34.bottom")}),-1.0]])]});
            var Q18;
            Q18=makeQuery(id+"F0.imprint","IMPRINT",FACE,{"disambiguationData":[TD([[makeQuery(id+"F0.imprint","IMPRINT",EDGE,{"derivedFrom":sQuery(id+"F0.wireOp",EDGE,"E42.bottom")}),-1.0]])]});
            var Q19;
            Q19=makeQuery(id+"F0.imprint","IMPRINT",FACE,{"disambiguationData":[TD([[makeQuery(id+"F0.imprint","IMPRINT",EDGE,{"derivedFrom":sQuery(id+"F0.wireOp",EDGE,"E50.bottom")}),-1.0]])]});
            var Q20;
            Q20=makeQuery(id+"F0.imprint","IMPRINT",FACE,{"disambiguationData":[TD([[makeQuery(id+"F0.imprint","IMPRINT",EDGE,{"derivedFrom":sQuery(id+"F0.wireOp",EDGE,"E60.bottom")}),-1.0]])]});
            var Q21;
            Q21=makeQuery(id+"F0.imprint","IMPRINT",FACE,{"disambiguationData":[TD([[makeQuery(id+"F0.imprint","IMPRINT",EDGE,{"derivedFrom":sQuery(id+"F0.wireOp",EDGE,"E68.bottom")}),-1.0]])]});
            var Q22;
            Q22=makeQuery(id+"F0.imprint","IMPRINT",FACE,{"disambiguationData":[TD([[makeQuery(id+"F0.imprint","IMPRINT",EDGE,{"derivedFrom":sQuery(id+"F0.wireOp",EDGE,"E77.bottom")}),-1.0]])]});
            var Q23;
            Q23=makeQuery(id+"F0.imprint","IMPRINT",FACE,{"disambiguationData":[TD([[makeQuery(id+"F0.imprint","IMPRINT",EDGE,{"derivedFrom":sQuery(id+"F0.wireOp",EDGE,"E83.bottom")}),-1.0]])]});
            var Q24;
            Q24=makeQuery(id+"F0.imprint","IMPRINT",FACE,{"disambiguationData":[TD([[makeQuery(id+"F0.imprint","IMPRINT",EDGE,{"derivedFrom":sQuery(id+"F0.wireOp",EDGE,"E89.bottom")}),-1.0]])]});
            var Q25;
            Q25=makeQuery(id+"F0.imprint","IMPRINT",FACE,{"disambiguationData":[TD([[makeQuery(id+"F0.imprint","IMPRINT",EDGE,{"derivedFrom":sQuery(id+"F0.wireOp",EDGE,"E95.bottom")}),-1.0]])]});
            var Q26;
            Q26=makeQuery(id+"F0.imprint","IMPRINT",FACE,{"disambiguationData":[TD([[makeQuery(id+"F0.imprint","IMPRINT",EDGE,{"derivedFrom":sQuery(id+"F0.wireOp",EDGE,"E106.bottom")}),-1.0]])]});
            var Q27;
            Q27=makeQuery(id+"F0.imprint","IMPRINT",FACE,{"disambiguationData":[TD([[makeQuery(id+"F0.imprint","IMPRINT",EDGE,{"derivedFrom":sQuery(id+"F0.wireOp",EDGE,"E115.bottom")}),-1.0]])]});
            var Q28;
            Q28=makeQuery(id+"F0.imprint","IMPRINT",FACE,{"disambiguationData":[TD([[makeQuery(id+"F0.imprint","IMPRINT",EDGE,{"derivedFrom":sQuery(id+"F0.wireOp",EDGE,"E124.bottom")}),-1.0]])]});
            var Q29;
            Q29=makeQuery(id+"F0.imprint","IMPRINT",FACE,{"disambiguationData":[TD([[makeQuery(id+"F0.imprint","IMPRINT",EDGE,{"derivedFrom":sQuery(id+"F0.wireOp",EDGE,"E125.bottom")}),-1.0]])]});
            var Q30;
            Q30=makeQuery(id+"F0.imprint","IMPRINT",FACE,{"disambiguationData":[TD([[makeQuery(id+"F0.imprint","IMPRINT",EDGE,{"derivedFrom":sQuery(id+"F0.wireOp",EDGE,"E133.bottom")}),-1.0]])]});
            var Q31;
            Q31=makeQuery(id+"F0.imprint","IMPRINT",FACE,{"disambiguationData":[TD([[makeQuery(id+"F0.imprint","IMPRINT",EDGE,{"derivedFrom":sQuery(id+"F0.wireOp",EDGE,"E141.bottom")}),-1.0]])]});
            var Q32;
            Q32=makeQuery(id+"F0.imprint","IMPRINT",FACE,{"disambiguationData":[TD([[makeQuery(id+"F0.imprint","IMPRINT",EDGE,{"derivedFrom":sQuery(id+"F0.wireOp",EDGE,"E149.bottom")}),-1.0]])]});
            var Q33;
            Q33=makeQuery(id+"F0.imprint","IMPRINT",FACE,{"disambiguationData":[TD([[makeQuery(id+"F0.imprint","IMPRINT",EDGE,{"derivedFrom":sQuery(id+"F0.wireOp",EDGE,"E157.bottom")}),-1.0]])]});
            var Q34;
            Q34=makeQuery(id+"F0.imprint","IMPRINT",FACE,{"disambiguationData":[TD([[makeQuery(id+"F0.imprint","IMPRINT",EDGE,{"derivedFrom":sQuery(id+"F0.wireOp",EDGE,"E165.bottom")}),-1.0]])]});
            var Q35;
            Q35=makeQuery(id+"F0.imprint","IMPRINT",FACE,{"disambiguationData":[TD([[makeQuery(id+"F0.imprint","IMPRINT",EDGE,{"derivedFrom":sQuery(id+"F0.wireOp",EDGE,"E166.bottom")}),-1.0]])]});
            var Q36;
            Q36=makeQuery(id+"F0.imprint","IMPRINT",FACE,{"disambiguationData":[TD([[makeQuery(id+"F0.imprint","IMPRINT",EDGE,{"derivedFrom":sQuery(id+"F0.wireOp",EDGE,"E167.bottom")}),-1.0]])]});
            var Q37;
            Q37=makeQuery(id+"F0.imprint","IMPRINT",FACE,{"disambiguationData":[TD([[makeQuery(id+"F0.imprint","IMPRINT",EDGE,{"derivedFrom":sQuery(id+"F0.wireOp",EDGE,"E168.bottom")}),-1.0]])]});
            var Q38;
            Q38=makeQuery(id+"F0.imprint","IMPRINT",FACE,{"disambiguationData":[TD([[makeQuery(id+"F0.imprint","IMPRINT",EDGE,{"derivedFrom":sQuery(id+"F0.wireOp",EDGE,"E169.bottom")}),-1.0]])]});
            var Q39;
            Q39=makeQuery(id+"F0.imprint","IMPRINT",FACE,{"disambiguationData":[TD([[makeQuery(id+"F0.imprint","IMPRINT",EDGE,{"derivedFrom":sQuery(id+"F0.wireOp",EDGE,"E170.bottom")}),-1.0]])]});
            var Q40;
            Q40=makeQuery(id+"F0.imprint","IMPRINT",FACE,{"disambiguationData":[TD([[makeQuery(id+"F0.imprint","IMPRINT",EDGE,{"derivedFrom":sQuery(id+"F0.wireOp",EDGE,"E171.bottom")}),-1.0]])]});
            var Q41;
            Q41=makeQuery(id+"F0.imprint","IMPRINT",FACE,{"disambiguationData":[TD([[makeQuery(id+"F0.imprint","IMPRINT",EDGE,{"derivedFrom":sQuery(id+"F0.wireOp",EDGE,"E172.bottom")}),-1.0]])]});
            var Q42;
            Q42=makeQuery(id+"F0.imprint","IMPRINT",FACE,{"disambiguationData":[TD([[makeQuery(id+"F0.imprint","IMPRINT",EDGE,{"derivedFrom":sQuery(id+"F0.wireOp",EDGE,"E173.bottom")}),-1.0]])]});
            var Q43;
            Q43=makeQuery(id+"F0.imprint","IMPRINT",FACE,{"disambiguationData":[TD([[makeQuery(id+"F0.imprint","IMPRINT",EDGE,{"derivedFrom":sQuery(id+"F0.wireOp",EDGE,"E174.bottom")}),-1.0]])]});
            var Q44;
            Q44=makeQuery(id+"F0.imprint","IMPRINT",FACE,{"disambiguationData":[TD([[makeQuery(id+"F0.imprint","IMPRINT",EDGE,{"derivedFrom":sQuery(id+"F0.wireOp",EDGE,"E175.bottom")}),-1.0]])]});
            var Q45;
            Q45=makeQuery(id+"F0.imprint","IMPRINT",FACE,{"disambiguationData":[TD([[makeQuery(id+"F0.imprint","IMPRINT",EDGE,{"derivedFrom":sQuery(id+"F0.wireOp",EDGE,"E176.bottom")}),-1.0]])]});
            extrude(context, id + "F1", {"entities" : qUnion([Q0, Q1, Q2, Q3, Q4, Q5, Q6, Q7, Q8, Q9, Q10, Q11, Q12, Q13, Q14, Q15, Q16, Q17, Q18, Q19, Q20, Q21, Q22, Q23, Q24, Q25, Q26, Q27, Q28, Q29, Q30, Q31, Q32, Q33, Q34, Q35, Q36, Q37, Q38, Q39, Q40, Q41, Q42, Q43, Q44, Q45]), "depth" : 3.17 * mm});
        }
    });
